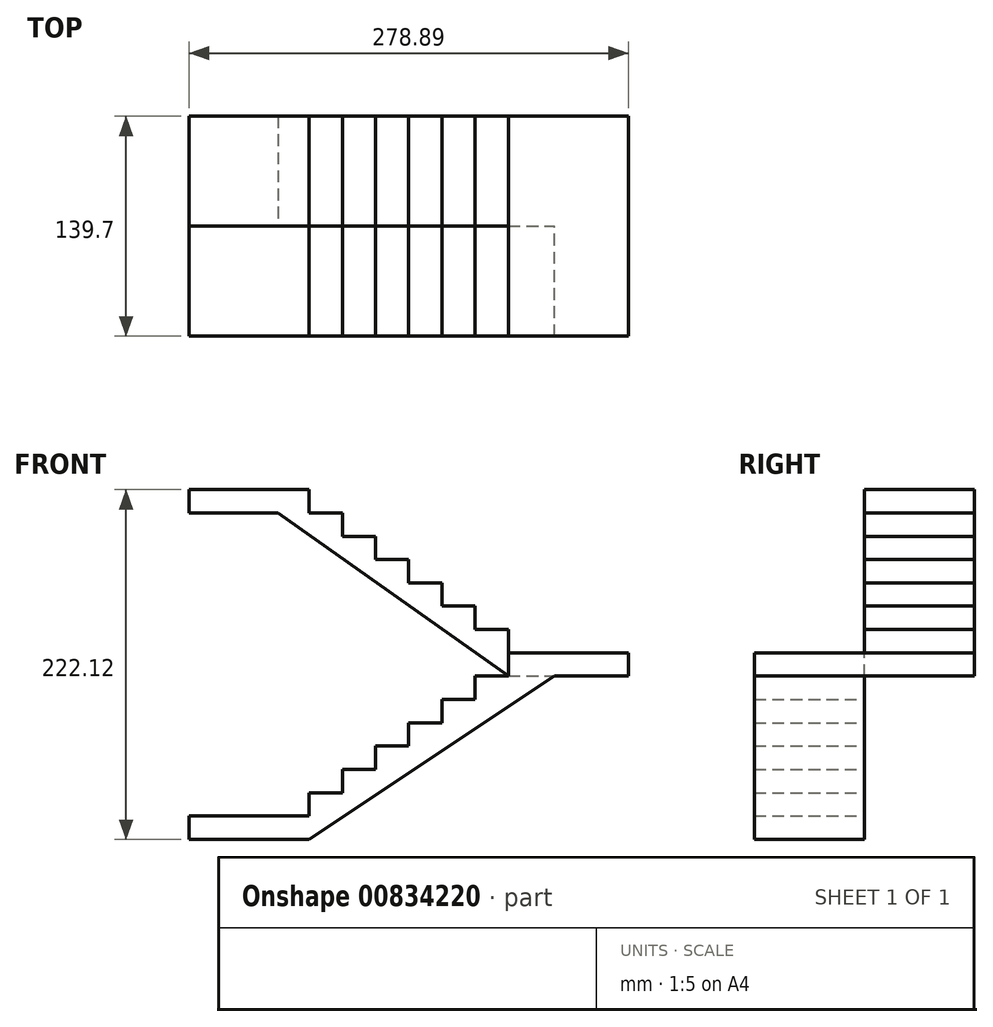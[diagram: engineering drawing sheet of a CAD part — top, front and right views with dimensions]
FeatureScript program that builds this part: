
annotation { "Feature Type Name" : "Feature", "Feature Type Description" : "" }
export const myFeature = defineFeature(function(context is Context, id is Id, definition is map)
    precondition{}
    {
        {
            var Q0;
            Q0=qCreatedBy(makeId("Front.planeOp"),FACE);
            var sketch = newSketch(context, id + "F0", { "sketchPlane" : qUnion([Q0])});
            skLineSegment(sketch, "E0", {"start": v(-132.52, -114.87) * mm, "end": v(-132.52, -100.07) * mm});
            skLineSegment(sketch, "E1", {"start": v(-132.52, -100.07) * mm, "end": v(-56.32, -100.07) * mm});
            skLineSegment(sketch, "E2", {"start": v(-56.32, -100.07) * mm, "end": v(-56.32, -85.26) * mm});
            skLineSegment(sketch, "E3", {"start": v(-56.32, -85.26) * mm, "end": v(-35.24, -85.26) * mm});
            skLineSegment(sketch, "E4", {"start": v(-35.24, -85.26) * mm, "end": v(-35.24, -70.45) * mm});
            skLineSegment(sketch, "E5", {"start": v(-35.24, -70.45) * mm, "end": v(-14.16, -70.45) * mm});
            skLineSegment(sketch, "E6", {"start": v(-14.16, -70.45) * mm, "end": v(-14.16, -55.64) * mm});
            skLineSegment(sketch, "E7", {"start": v(-14.16, -55.64) * mm, "end": v(6.92, -55.64) * mm});
            skLineSegment(sketch, "E8", {"start": v(6.92, -55.64) * mm, "end": v(6.92, -40.83) * mm});
            skLineSegment(sketch, "E9", {"start": v(6.92, -40.83) * mm, "end": v(28, -40.83) * mm});
            skLineSegment(sketch, "E10", {"start": v(28, -40.83) * mm, "end": v(28, -26.02) * mm});
            skLineSegment(sketch, "E11", {"start": v(28, -26.02) * mm, "end": v(49.09, -26.02) * mm});
            skLineSegment(sketch, "E12", {"start": v(49.09, -26.02) * mm, "end": v(49.09, -11.22) * mm});
            skLineSegment(sketch, "E13", {"start": v(49.09, -11.22) * mm, "end": v(70.17, -11.22) * mm});
            skLineSegment(sketch, "E14", {"start": v(70.17, -11.22) * mm, "end": v(70.17, 3.6) * mm});
            skLineSegment(sketch, "E15", {"start": v(70.17, 3.6) * mm, "end": v(146.37, 3.6) * mm});
            skLineSegment(sketch, "E16", {"start": v(70.17, 3.6) * mm, "end": v(70.17, 18.4) * mm});
            skLineSegment(sketch, "E17", {"start": v(70.17, 18.4) * mm, "end": v(49.09, 18.4) * mm});
            skLineSegment(sketch, "E18", {"start": v(49.09, 18.4) * mm, "end": v(49.09, 33.2) * mm});
            skLineSegment(sketch, "E19", {"start": v(49.09, 33.2) * mm, "end": v(28, 33.2) * mm});
            skLineSegment(sketch, "E20", {"start": v(28, 33.2) * mm, "end": v(28, 48.02) * mm});
            skLineSegment(sketch, "E21", {"start": v(28, 48.02) * mm, "end": v(6.92, 48.02) * mm});
            skLineSegment(sketch, "E22", {"start": v(6.92, 48.02) * mm, "end": v(6.92, 62.82) * mm});
            skLineSegment(sketch, "E23", {"start": v(6.92, 62.82) * mm, "end": v(-14.16, 62.82) * mm});
            skLineSegment(sketch, "E24", {"start": v(-14.16, 62.82) * mm, "end": v(-14.16, 77.63) * mm});
            skLineSegment(sketch, "E25", {"start": v(-14.16, 77.63) * mm, "end": v(-35.24, 77.63) * mm});
            skLineSegment(sketch, "E26", {"start": v(-35.24, 77.63) * mm, "end": v(-35.24, 92.44) * mm});
            skLineSegment(sketch, "E27", {"start": v(-35.24, 92.44) * mm, "end": v(-56.32, 92.44) * mm});
            skLineSegment(sketch, "E28", {"start": v(-56.32, 92.44) * mm, "end": v(-56.32, 107.25) * mm});
            skLineSegment(sketch, "E29", {"start": v(-56.32, 107.25) * mm, "end": v(-132.52, 107.25) * mm});
            skLineSegment(sketch, "E30", {"start": v(146.37, 3.6) * mm, "end": v(146.37, -11.22) * mm});
            skLineSegment(sketch, "E31", {"start": v(146.37, -11.22) * mm, "end": v(99.58, -11.22) * mm});
            skLineSegment(sketch, "E32", {"start": v(-132.52, -114.87) * mm, "end": v(-56.32, -114.87) * mm});
            skLineSegment(sketch, "E33", {"start": v(-56.32, -114.87) * mm, "end": v(99.58, -11.22) * mm});
            skLineSegment(sketch, "E34", {"start": v(-132.52, 107.25) * mm, "end": v(-132.52, 92.44) * mm});
            skLineSegment(sketch, "E35", {"start": v(-132.52, 92.44) * mm, "end": v(-76.2, 92.44) * mm});
            skLineSegment(sketch, "E36", {"start": v(70.17, -11.22) * mm, "end": v(-76.2, 92.44) * mm});
            skLineSegment(sketch, "E37", {"start": v(70.17, -11.22) * mm, "end": v(99.58, -11.22) * mm});
            skSolve(sketch);
        }
        {
            var Q0;
            Q0=makeQuery(id+"F0.imprint","IMPRINT",FACE,{"disambiguationData":[TD([[makeQuery(id+"F0.imprint","IMPRINT",EDGE,{"derivedFrom":sQuery(id+"F0.wireOp",EDGE,"E0")}),-1.0]])]});
            var Q1;
            Q1=makeQuery(id+"F0.imprint","IMPRINT",FACE,{"disambiguationData":[TD([[makeQuery(id+"F0.imprint","IMPRINT",EDGE,{"derivedFrom":sQuery(id+"F0.wireOp",EDGE,"E14")}),-1.0]])]});
            extrude(context, id + "F1", {"entities" : qUnion([Q0, Q1]), "depth" : 69.85 * mm, "offsetDistance" : 25.4 * mm});
        }
        {
            var Q0;
            Q0=makeQuery(id+"F0.imprint","IMPRINT",FACE,{"disambiguationData":[TD([[makeQuery(id+"F0.imprint","IMPRINT",EDGE,{"derivedFrom":sQuery(id+"F0.wireOp",EDGE,"E14")}),1.0]])]});
            var Q1;
            Q1=makeQuery(id+"F0.imprint","IMPRINT",FACE,{"disambiguationData":[TD([[makeQuery(id+"F0.imprint","IMPRINT",EDGE,{"derivedFrom":sQuery(id+"F0.wireOp",EDGE,"E14")}),-1.0]])]});
            extrude(context, id + "F2", {"entities" : qUnion([Q0, Q1]), "operationType" : NewBodyOperationType.ADD, "oppositeDirection" : true, "depth" : 69.85 * mm, "offsetDistance" : 25.4 * mm});
        }
    });
